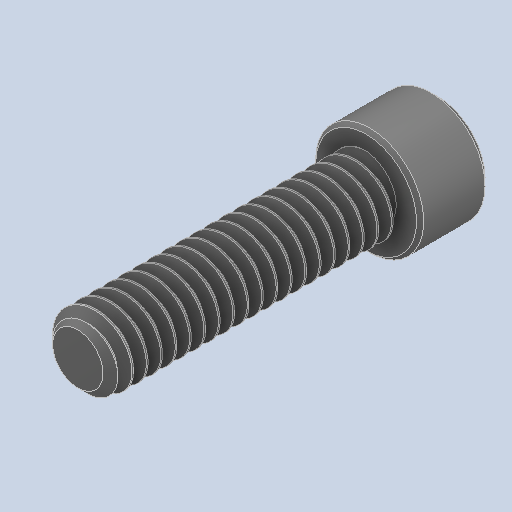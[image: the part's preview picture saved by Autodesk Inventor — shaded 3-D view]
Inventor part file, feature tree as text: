
AUTODESK INVENTOR PART (.ipt)
format: ipt  version: 2023.2 (Build 272271000, 271)  size: 709,120 bytes
history: native  units: in
note: dims shown in document units (in); Inventor stores cm internally (conversion verified against a paired STEP export)
features: chamfer x1
ambient origin geometry x8: Origin, YZ Plane, XZ Plane, XY Plane, X Axis, Y Axis, Z Axis, Center Point
bodies: Solid1 (feature_tree)
feature tree (1):
  chamfer  "Chamfer2"  [1 undecoded]
note: 1 required parameter value undecoded (feature->parameter linkage not recoverable at this tier; creation-order binding heuristic only, values carry confidence <= 0.55)
